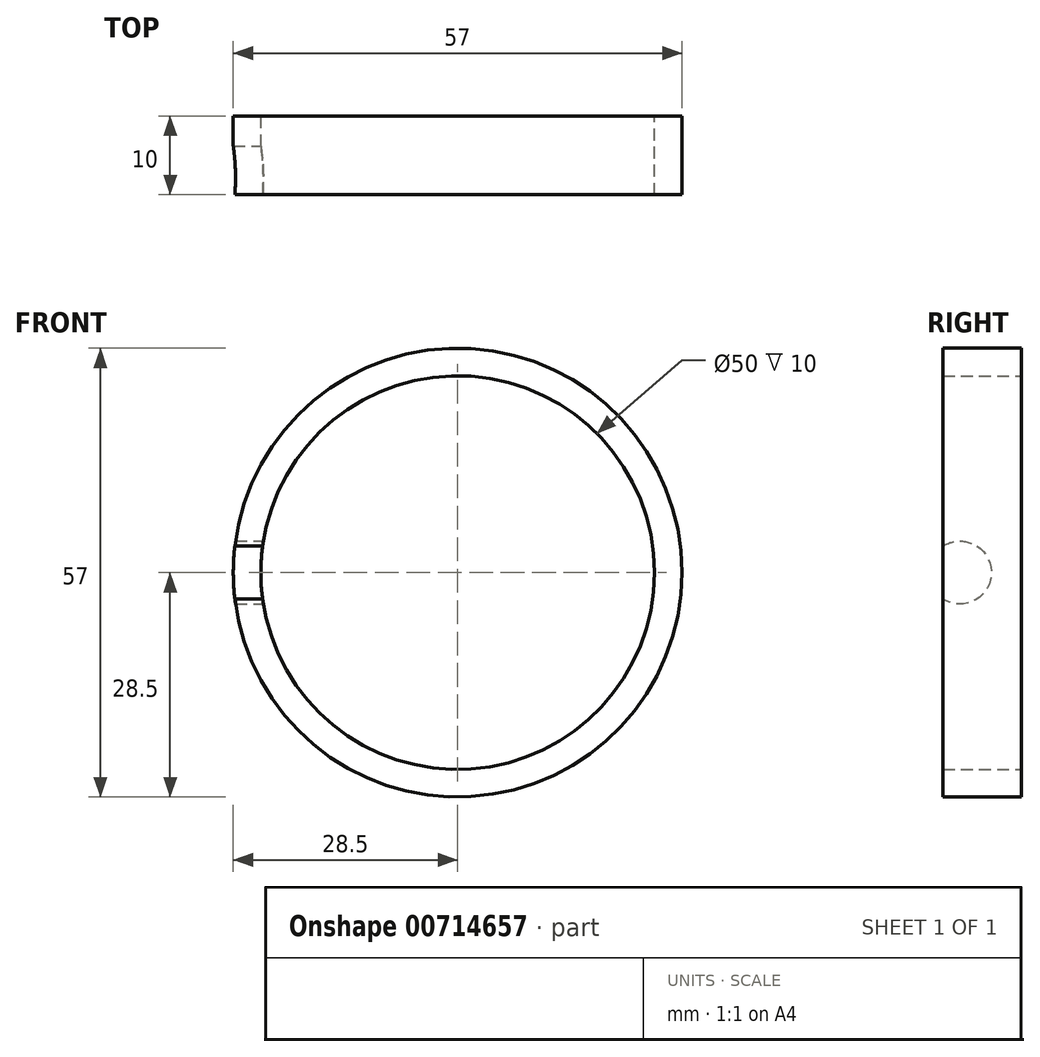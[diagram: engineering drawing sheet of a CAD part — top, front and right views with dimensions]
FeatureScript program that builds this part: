
annotation { "Feature Type Name" : "Feature", "Feature Type Description" : "" }
export const myFeature = defineFeature(function(context is Context, id is Id, definition is map)
    precondition{}
    {
        {
            var Q0;
            Q0=qCreatedBy(makeId("Front.planeOp"),FACE);
            var sketch = newSketch(context, id + "F0", { "sketchPlane" : qUnion([Q0])});
            skCircle(sketch, "E0", {"center": v(0, 0) * mm, "radius": 25 * mm});
            skCircle(sketch, "E1", {"center": v(0, 0) * mm, "radius": 28.5 * mm});
            skSolve(sketch);
        }
        {
            var Q0;
            Q0=makeQuery(id+"F0.imprint","IMPRINT",FACE,{"disambiguationData":[TD([[makeQuery(id+"F0.imprint","IMPRINT",EDGE,{"derivedFrom":sQuery(id+"F0.wireOp",EDGE,"E0")}),-1.0]])]});
            extrude(context, id + "F1", {"entities" : qUnion([Q0]), "depth" : 10 * mm, "offsetDistance" : 25 * mm});
        }
        {
            var Q0;
            Q0=qCreatedBy(makeId("Right.planeOp"),FACE);
            var sketch = newSketch(context, id + "F2", { "sketchPlane" : qUnion([Q0])});
            skPoint(sketch, "E2", {"position": v(-7.83, 0) * mm});
            skSolve(sketch);
        }
        {
            var Q0;
            Q0=sQuery(id+"F2.wireOp",VERTEX,"E2");
            var Q1;
            Q1=makeQuery(id+"F1.opExtrude","SWEPT_BODY",BODY,{"disambiguationData":[OSD([sQuery(id+"F0.wireOp",EDGE,"E0"),sQuery(id+"F0.wireOp",EDGE,"E1")])]});
            hole(context, id + "F3", {"style" : HoleStyle.SIMPLE, "endStyle" : HoleEndStyle.THROUGH, "holeDiameter" : 8 * mm, "majorDiameter" : 5 * mm, "isTappedThrough" : true, "tappedDepth" : 12 * mm, "tapClearance" : 3, "startFromSketch" : true, "locations" : qUnion([Q0]), "scope" : qUnion([Q1])});
        }
    });
